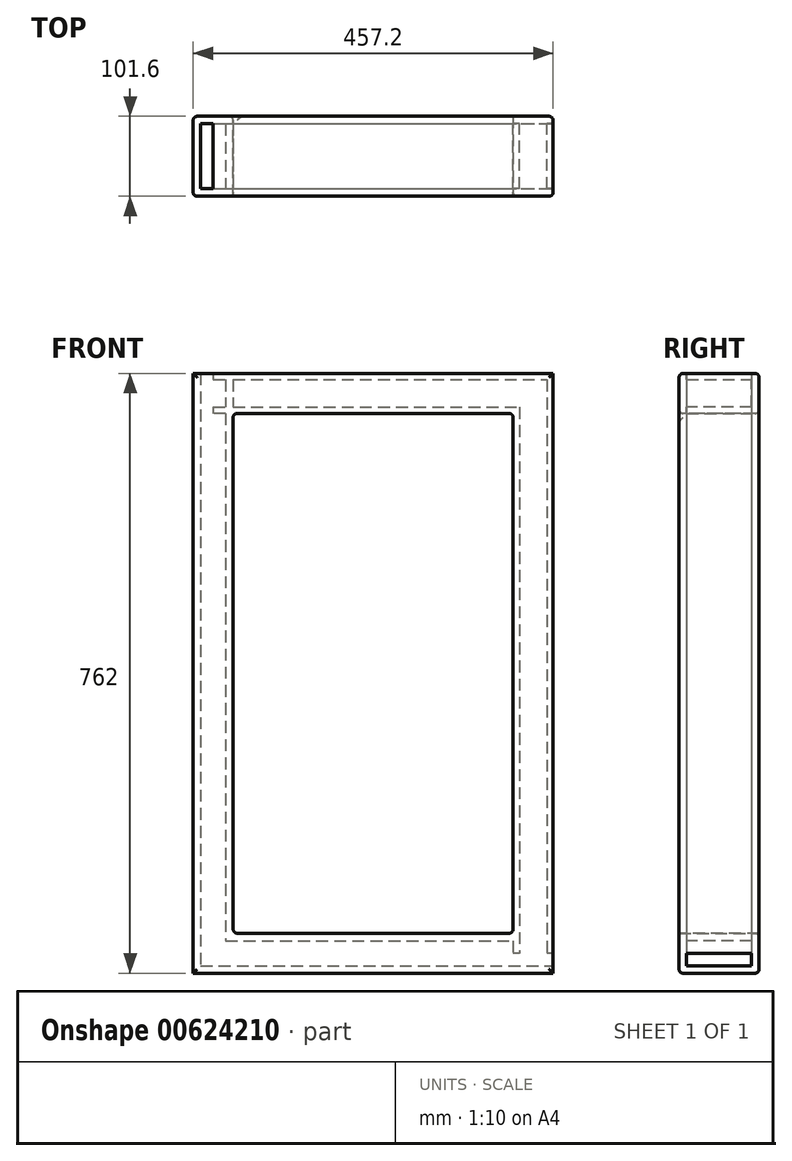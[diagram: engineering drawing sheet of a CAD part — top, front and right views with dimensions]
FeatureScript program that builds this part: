
annotation { "Feature Type Name" : "Feature", "Feature Type Description" : "" }
export const myFeature = defineFeature(function(context is Context, id is Id, definition is map)
    precondition{}
    {
        {
            var Q0;
            Q0=qCreatedBy(makeId("Front.planeOp"),FACE);
            var sketch = newSketch(context, id + "F0", { "sketchPlane" : qUnion([Q0])});
            skLineSegment(sketch, "E0.bottom", {"start": v(0, 0) * mm, "end": v(406.4, 0) * mm});
            skLineSegment(sketch, "E0.top", {"start": v(0, -711.2) * mm, "end": v(406.4, -711.2) * mm});
            skLineSegment(sketch, "E0.left", {"start": v(0, 0) * mm, "end": v(0, -711.2) * mm});
            skLineSegment(sketch, "E0.right", {"start": v(406.4, 0) * mm, "end": v(406.4, -711.2) * mm});
            skSolve(sketch);
        }
        {
            var Q0;
            Q0=qCreatedBy(makeId("Right.planeOp"),FACE);
            var sketch = newSketch(context, id + "F1", { "sketchPlane" : qUnion([Q0])});
            skLineSegment(sketch, "E1.bottom", {"start": v(-50.8, 25.4) * mm, "end": v(50.8, 25.4) * mm});
            skLineSegment(sketch, "E1.top", {"start": v(-50.8, -25.4) * mm, "end": v(50.8, -25.4) * mm});
            skLineSegment(sketch, "E1.left", {"start": v(-50.8, 25.4) * mm, "end": v(-50.8, -25.4) * mm});
            skLineSegment(sketch, "E1.right", {"start": v(50.8, 25.4) * mm, "end": v(50.8, -25.4) * mm});
            skPoint(sketch, "E1.middle", {"position": v(0, 0) * mm});
            skLineSegment(sketch, "E2.bottom", {"start": v(-41.28, 17.44) * mm, "end": v(41.28, 17.44) * mm});
            skLineSegment(sketch, "E2.top", {"start": v(-41.28, -17.44) * mm, "end": v(41.28, -17.44) * mm});
            skLineSegment(sketch, "E2.left", {"start": v(-41.28, 17.44) * mm, "end": v(-41.28, -17.44) * mm});
            skLineSegment(sketch, "E2.right", {"start": v(41.28, 17.44) * mm, "end": v(41.28, -17.44) * mm});
            skSolve(sketch);
        }
        {
            var Q0;
            Q0=makeQuery(id+"F1.imprint","IMPRINT",FACE,{"disambiguationData":[TD([[makeQuery(id+"F1.imprint","IMPRINT",EDGE,{"derivedFrom":sQuery(id+"F1.wireOp",EDGE,"E1.bottom")}),-1.0]])]});
            var Q1;
            Q1=sQuery(id+"F0.wireOp",EDGE,"E0.bottom");
            var Q2;
            Q2=sQuery(id+"F0.wireOp",EDGE,"E0.right");
            sweep(context, id + "F2", {"profiles" : qUnion([Q0]), "path" : qUnion([Q1, Q2])});
        }
        {
            var Q0;
            Q0=qCreatedBy(makeId("Top.planeOp"),FACE);
            cPlane(context, id + "F3", {"entities" : qUnion([Q0]), "cplaneType" : CPlaneType.OFFSET, "offset" : 25.4 * mm, "width" : 152.4 * mm, "height" : 152.4 * mm});
        }
        {
            var Q0;
            Q0=qCreatedBy(id+"F3.planeOp",FACE);
            var sketch = newSketch(context, id + "F4", { "sketchPlane" : qUnion([Q0])});
            skLineSegment(sketch, "E3.bottom", {"start": v(-25.4, 50.8) * mm, "end": v(25.4, 50.8) * mm});
            skLineSegment(sketch, "E3.top", {"start": v(-25.4, -50.8) * mm, "end": v(25.4, -50.8) * mm});
            skLineSegment(sketch, "E3.left", {"start": v(-25.4, 50.8) * mm, "end": v(-25.4, -50.8) * mm});
            skLineSegment(sketch, "E3.right", {"start": v(25.4, 50.8) * mm, "end": v(25.4, -50.8) * mm});
            skPoint(sketch, "E3.middle", {"position": v(0, 0) * mm});
            skLineSegment(sketch, "E4.bottom", {"start": v(15.88, 41.27) * mm, "end": v(-15.88, 41.27) * mm});
            skLineSegment(sketch, "E4.top", {"start": v(15.88, -41.27) * mm, "end": v(-15.88, -41.27) * mm});
            skLineSegment(sketch, "E4.left", {"start": v(15.88, 41.27) * mm, "end": v(15.88, -41.27) * mm});
            skLineSegment(sketch, "E4.right", {"start": v(-15.88, 41.27) * mm, "end": v(-15.88, -41.27) * mm});
            skSolve(sketch);
        }
        {
            var Q0;
            Q0=makeQuery(id+"F4.imprint","IMPRINT",FACE,{"disambiguationData":[TD([[makeQuery(id+"F4.imprint","IMPRINT",EDGE,{"derivedFrom":sQuery(id+"F4.wireOp",EDGE,"E3.bottom")}),-1.0]])]});
            var Q1;
            Q1=sQuery(id+"F0.wireOp",EDGE,"E0.left");
            var Q2;
            Q2=sQuery(id+"F0.wireOp",EDGE,"E0.top");
            sweep(context, id + "F5", {"operationType" : NewBodyOperationType.ADD, "profiles" : qUnion([Q0]), "path" : qUnion([Q1, Q2])});
        }
        {
            var Q0;
            Q0=makeQuery(id+"F5.opSweep","CAP_FACE",FACE,{"disambiguationData":[OSD([sQuery(id+"F0.wireOp",VERTEX,"E0.top.end"),sQuery(id+"F4.wireOp",EDGE,"E3.bottom"),sQuery(id+"F4.wireOp",EDGE,"E3.top"),sQuery(id+"F4.wireOp",EDGE,"E3.left"),sQuery(id+"F4.wireOp",EDGE,"E3.right"),sQuery(id+"F4.wireOp",EDGE,"E4.bottom"),sQuery(id+"F4.wireOp",EDGE,"E4.top"),sQuery(id+"F4.wireOp",EDGE,"E4.left"),sQuery(id+"F4.wireOp",EDGE,"E4.right")])],"isStart":false});
            extrude(context, id + "F6", {"entities" : qUnion([Q0]), "operationType" : NewBodyOperationType.ADD, "depth" : 50.8 * mm, "offsetDistance" : 25.4 * mm});
        }
        {
            var Q0;
            Q0=makeQuery(id+"F5.opSweep","CAP_EDGE",EDGE,{"disambiguationData":[OSD([sQuery(id+"F0.wireOp",VERTEX,"E0.top.end"),sQuery(id+"F4.wireOp",EDGE,"E3.right")])],"isStart":false});
            var Q1;
            Q1=makeQuery(id+"F5.opSweep","MID_CAP_EDGE",EDGE,{"disambiguationData":[OSD([sQuery(id+"F0.wireOp",VERTEX,"E0.top.start"),sQuery(id+"F4.wireOp",EDGE,"E3.right")])],"capPos":1.0});
            var Q2;
            Q2=makeQuery(id+"F5.boolean.opBoolean","INTERSECT",EDGE,{"derivedFrom":[makeQuery(id+"F2.opSweep","SWEPT_FACE",FACE,{"disambiguationData":[OSD([sQuery(id+"F0.wireOp",EDGE,"E0.bottom"),sQuery(id+"F1.wireOp",EDGE,"E1.top")])]}),makeQuery(id+"F5.opSweep","SWEPT_FACE",FACE,{"disambiguationData":[OSD([sQuery(id+"F0.wireOp",EDGE,"E0.left"),sQuery(id+"F4.wireOp",EDGE,"E3.right")])]})]});
            var Q3;
            Q3=makeQuery(id+"F2.opSweep","MID_CAP_EDGE",EDGE,{"disambiguationData":[OSD([sQuery(id+"F0.wireOp",VERTEX,"E0.right.start"),sQuery(id+"F1.wireOp",EDGE,"E1.top")])],"capPos":1.0});
            var Q4;
            Q4=makeQuery(id+"F2.opSweep","SWEPT_EDGE",EDGE,{"disambiguationData":[OSD([sQuery(id+"F0.wireOp",EDGE,"E0.bottom"),sQuery(id+"F1.wireOp",EDGE,"E1.top"),sQuery(id+"F1.wireOp",EDGE,"E1.left")])]});
            var Q5;
            Q5=makeQuery(id+"F5.opSweep","SWEPT_EDGE",EDGE,{"disambiguationData":[OSD([sQuery(id+"F0.wireOp",EDGE,"E0.left"),sQuery(id+"F4.wireOp",EDGE,"E3.bottom"),sQuery(id+"F4.wireOp",EDGE,"E3.right")])]});
            fillet(context, id + "F7", {"entities" : qUnion([Q0, Q1, Q2, Q3, Q4, Q5]), "radius" : 5.08 * mm, "tangentPropagation" : true, "allowEdgeOverflow" : false});
        }
        {
            var Q0;
            Q0=makeQuery(id+"F5.boolean.opBoolean","MERGE",EDGE,{"derivedFrom":[makeQuery(id+"F2.opSweep","SWEPT_EDGE",EDGE,{"disambiguationData":[OSD([sQuery(id+"F0.wireOp",EDGE,"E0.bottom"),sQuery(id+"F1.wireOp",EDGE,"E1.bottom"),sQuery(id+"F1.wireOp",EDGE,"E1.left")])]}),makeQuery(id+"F5.opSweep","CAP_EDGE",EDGE,{"disambiguationData":[OSD([sQuery(id+"F0.wireOp",VERTEX,"E0.left.start"),sQuery(id+"F4.wireOp",EDGE,"E3.top")])],"isStart":true})]});
            var Q1;
            Q1=makeQuery(id+"F5.opSweep","SWEPT_EDGE",EDGE,{"disambiguationData":[OSD([sQuery(id+"F0.wireOp",EDGE,"E0.left"),sQuery(id+"F4.wireOp",EDGE,"E3.top"),sQuery(id+"F4.wireOp",EDGE,"E3.left")])]});
            var Q2;
            Q2=makeQuery(id+"F6.boolean.opBoolean","MERGE",EDGE,{"derivedFrom":[makeQuery(id+"F2.opSweep","SWEPT_EDGE",EDGE,{"disambiguationData":[OSD([sQuery(id+"F0.wireOp",EDGE,"E0.right"),sQuery(id+"F1.wireOp",EDGE,"E1.bottom"),sQuery(id+"F1.wireOp",EDGE,"E1.left")])]}),makeQuery(id+"F6.opExtrude","CAP_EDGE",EDGE,{"disambiguationData":[OSD([sQuery(id+"F0.wireOp",VERTEX,"E0.top.end"),sQuery(id+"F4.wireOp",EDGE,"E3.top")])],"isStart":false})]});
            var Q3;
            {var subQ0=sQuery(id+"F4.wireOp",EDGE,"E3.left");var subQ1=sQuery(id+"F4.wireOp",EDGE,"E3.top");var subQ2=sQuery(id+"F0.wireOp",EDGE,"E0.top");Q3=makeQuery(id+"F6.boolean.opBoolean","MERGE",EDGE,{"derivedFrom":[makeQuery(id+"F5.opSweep","SWEPT_EDGE",EDGE,{"disambiguationData":[OSD([subQ2,subQ1,subQ0])]}),makeQuery(id+"F6.opExtrude","SWEPT_EDGE",EDGE,{"disambiguationData":[OSD([subQ2,subQ1,subQ0])]})]});}
            var Q4;
            Q4=makeQuery(id+"F5.opSweep","SWEPT_EDGE",EDGE,{"disambiguationData":[OSD([sQuery(id+"F0.wireOp",EDGE,"E0.left"),sQuery(id+"F4.wireOp",EDGE,"E3.bottom"),sQuery(id+"F4.wireOp",EDGE,"E3.left")])]});
            var Q5;
            {var subQ0=sQuery(id+"F4.wireOp",EDGE,"E3.left");var subQ1=sQuery(id+"F4.wireOp",EDGE,"E3.bottom");var subQ2=sQuery(id+"F0.wireOp",EDGE,"E0.top");Q5=makeQuery(id+"F6.boolean.opBoolean","MERGE",EDGE,{"derivedFrom":[makeQuery(id+"F5.opSweep","SWEPT_EDGE",EDGE,{"disambiguationData":[OSD([subQ2,subQ1,subQ0])]}),makeQuery(id+"F6.opExtrude","SWEPT_EDGE",EDGE,{"disambiguationData":[OSD([subQ2,subQ1,subQ0])]})]});}
            var Q6;
            Q6=makeQuery(id+"F6.boolean.opBoolean","MERGE",EDGE,{"derivedFrom":[makeQuery(id+"F2.opSweep","SWEPT_EDGE",EDGE,{"disambiguationData":[OSD([sQuery(id+"F0.wireOp",EDGE,"E0.right"),sQuery(id+"F1.wireOp",EDGE,"E1.bottom"),sQuery(id+"F1.wireOp",EDGE,"E1.right")])]}),makeQuery(id+"F6.opExtrude","CAP_EDGE",EDGE,{"disambiguationData":[OSD([sQuery(id+"F0.wireOp",VERTEX,"E0.top.end"),sQuery(id+"F4.wireOp",EDGE,"E3.bottom")])],"isStart":false})]});
            var Q7;
            Q7=makeQuery(id+"F5.boolean.opBoolean","MERGE",EDGE,{"derivedFrom":[makeQuery(id+"F2.opSweep","SWEPT_EDGE",EDGE,{"disambiguationData":[OSD([sQuery(id+"F0.wireOp",EDGE,"E0.bottom"),sQuery(id+"F1.wireOp",EDGE,"E1.bottom"),sQuery(id+"F1.wireOp",EDGE,"E1.right")])]}),makeQuery(id+"F5.opSweep","CAP_EDGE",EDGE,{"disambiguationData":[OSD([sQuery(id+"F0.wireOp",VERTEX,"E0.left.start"),sQuery(id+"F4.wireOp",EDGE,"E3.bottom")])],"isStart":true})]});
            fillet(context, id + "F8", {"entities" : qUnion([Q0, Q1, Q2, Q3, Q4, Q5, Q6, Q7]), "radius" : 5.08 * mm, "tangentPropagation" : true, "allowEdgeOverflow" : false});
        }
    });
